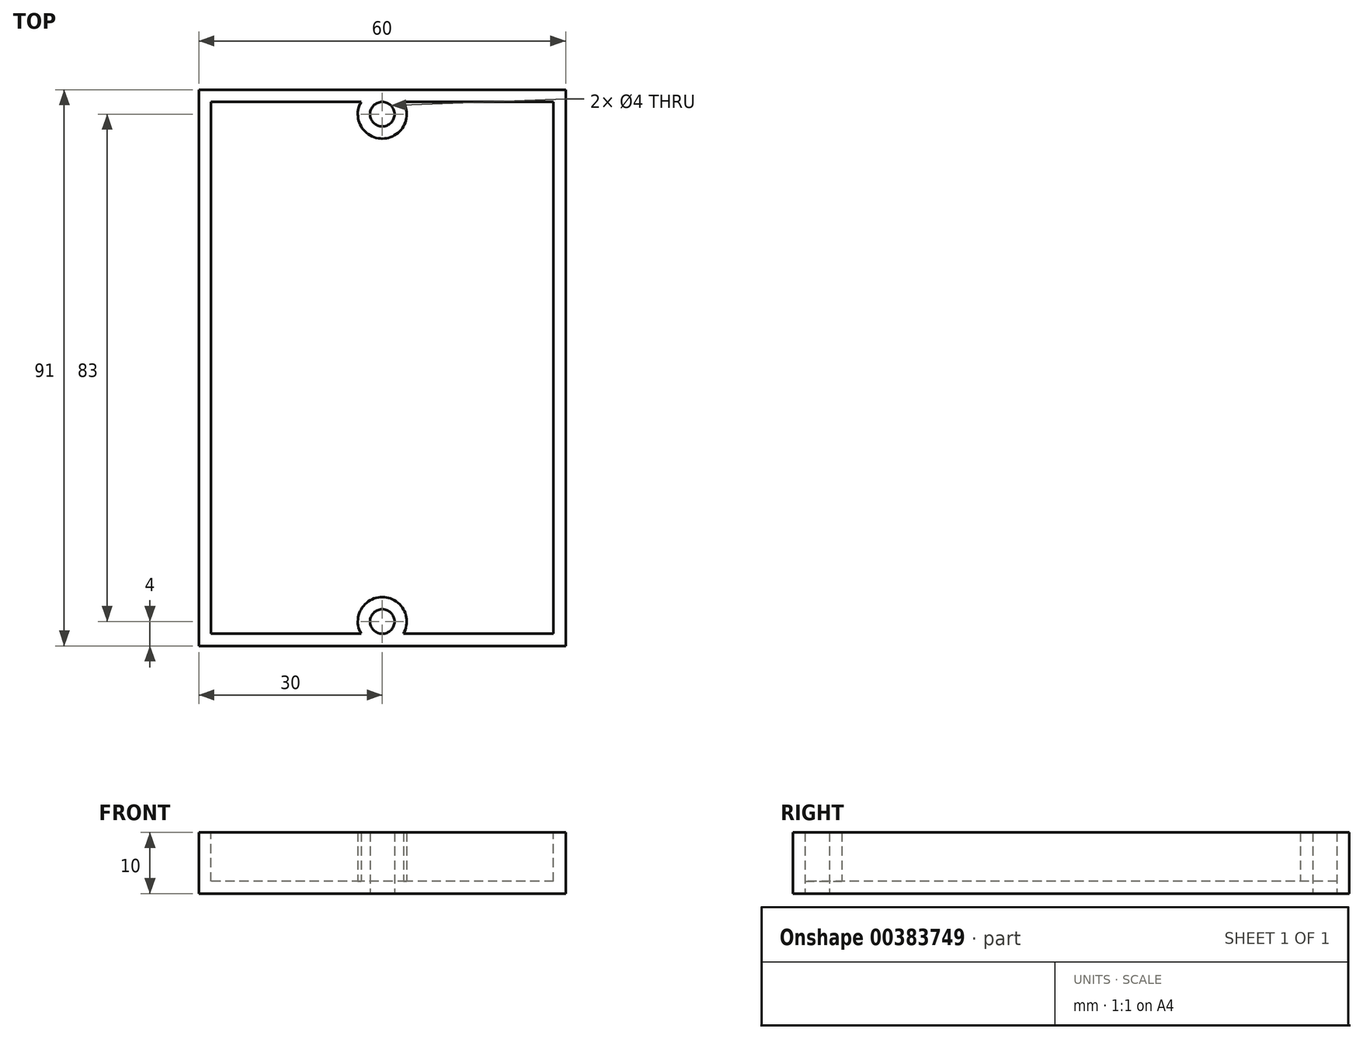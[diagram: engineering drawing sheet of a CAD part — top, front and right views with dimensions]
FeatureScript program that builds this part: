
annotation { "Feature Type Name" : "Feature", "Feature Type Description" : "" }
export const myFeature = defineFeature(function(context is Context, id is Id, definition is map)
    precondition{}
    {
        {
            assignVariable(context, id + "F0", {"name" : "lidwallthickness", "anyValue" : 2});
        }
        {
            assignVariable(context, id + "F1", {"name" : "lidheight", "anyValue" : 10});
        }
        {
            var Q0;
            Q0=qCreatedBy(makeId("Top.planeOp"),FACE);
            var sketch = newSketch(context, id + "F2", { "sketchPlane" : qUnion([Q0])});
            skLineSegment(sketch, "E0.bottom", {"start": v(30, 45.5) * mm, "end": v(-30, 45.5) * mm});
            skLineSegment(sketch, "E0.top", {"start": v(30, -45.5) * mm, "end": v(-30, -45.5) * mm});
            skLineSegment(sketch, "E0.left", {"start": v(30, 45.5) * mm, "end": v(30, -45.5) * mm});
            skLineSegment(sketch, "E0.right", {"start": v(-30, 45.5) * mm, "end": v(-30, -45.5) * mm});
            skPoint(sketch, "E0.middle", {"position": v(0, 0) * mm});
            skSolve(sketch);
        }
        {
            var Q0;
            Q0 = qSketchRegion(id + "F2", true);
            extrude(context, id + "F3", {"entities" : qUnion([Q0]), "depth" : (getVariable(context, 'lidheight')) * mm});
        }
        {
            var Q0;
            Q0=makeQuery(id+"F3.opExtrude","CAP_FACE",FACE,{"disambiguationData":[OSD([sQuery(id+"F2.wireOp",EDGE,"E0.bottom"),sQuery(id+"F2.wireOp",EDGE,"E0.top"),sQuery(id+"F2.wireOp",EDGE,"E0.left"),sQuery(id+"F2.wireOp",EDGE,"E0.right")])],"isStart":false});
            var sketch = newSketch(context, id + "F4", { "sketchPlane" : qUnion([Q0])});
            skLineSegment(sketch, "E1.bottom", {"start": v(28, 43.5) * mm, "end": v(-28, 43.5) * mm});
            skLineSegment(sketch, "E1.top", {"start": v(28, -43.5) * mm, "end": v(-28, -43.5) * mm});
            skLineSegment(sketch, "E1.left", {"start": v(28, 43.5) * mm, "end": v(28, -43.5) * mm});
            skLineSegment(sketch, "E1.right", {"start": v(-28, 43.5) * mm, "end": v(-28, -43.5) * mm});
            skPoint(sketch, "E1.middle", {"position": v(0, 0) * mm});
            skSolve(sketch);
        }
        {
            var Q0;
            Q0 = qSketchRegion(id + "F4", true);
            extrude(context, id + "F5", {"entities" : qUnion([Q0]), "operationType" : NewBodyOperationType.REMOVE, "oppositeDirection" : true, "depth" : (getVariable(context, 'lidheight') - getVariable(context, 'lidwallthickness')) * mm});
        }
        {
            var Q0;
            Q0=makeQuery(id+"F3.opExtrude","CAP_FACE",FACE,{"disambiguationData":[OSD([sQuery(id+"F2.wireOp",EDGE,"E0.bottom"),sQuery(id+"F2.wireOp",EDGE,"E0.top"),sQuery(id+"F2.wireOp",EDGE,"E0.left"),sQuery(id+"F2.wireOp",EDGE,"E0.right")])],"isStart":true});
            var sketch = newSketch(context, id + "F6", { "sketchPlane" : qUnion([Q0])});
            skCircle(sketch, "E2", {"center": v(0, -41.5) * mm, "radius": 4 * mm});
            skCircle(sketch, "E3.MirrorC", {"center": v(0, 41.5) * mm, "radius": 4 * mm});
            skSolve(sketch);
        }
        {
            var Q0;
            Q0 = qSketchRegion(id + "F6", true);
            extrude(context, id + "F7", {"entities" : qUnion([Q0]), "operationType" : NewBodyOperationType.ADD, "oppositeDirection" : true, "depth" : (getVariable(context, 'lidheight')) * mm});
        }
        {
            var Q0;
            Q0=makeQuery(id+"F3.opExtrude","CAP_FACE",FACE,{"disambiguationData":[OSD([sQuery(id+"F2.wireOp",EDGE,"E0.bottom"),sQuery(id+"F2.wireOp",EDGE,"E0.top"),sQuery(id+"F2.wireOp",EDGE,"E0.left"),sQuery(id+"F2.wireOp",EDGE,"E0.right")])],"isStart":true});
            var sketch = newSketch(context, id + "F8", { "sketchPlane" : qUnion([Q0])});
            skCircle(sketch, "E4", {"center": v(0, -41.5) * mm, "radius": 2 * mm});
            skPoint(sketch, "E4.centerSnap0", {"position": v(0, -45.5) * mm});
            skCircle(sketch, "E5.MirrorC", {"center": v(0, 41.5) * mm, "radius": 2 * mm});
            skSolve(sketch);
        }
        {
            var Q0;
            Q0 = qSketchRegion(id + "F8", true);
            extrude(context, id + "F9", {"entities" : qUnion([Q0]), "operationType" : NewBodyOperationType.REMOVE, "endBound" : BoundingType.THROUGH_ALL, "oppositeDirection" : true, "depth" : 25 * mm});
        }
    });
